# Revit family: Louver-Channel_Frame-Carnes-Rectangular-Motorized_Damper_FPJB
name_source: partatom
category: Air Terminals
revit_build: Autodesk Revit MEP 2012 (Build: 20110916_2132(x64)
units: mm (PartAtom-declared; Revit-internal decimal feet)

## types (1)
- (See Type Catalog)
    04 CSI = 08 91 00
    95 CSI = 10200
    Airflow = 0 CFM
    Assembly Code = D3090700
    Blade Material = Aluminum - Carnes - Extruded
    Catalog URL = http://www.carnes.com
    Connector Description 1 = Duct Connetor
    Default Elevation = 48"
    Description = Combination Louver / Damper
    Frame Material = Aluminum - Carnes - Extruded
    Free Area = 0 SF
    Free Area Note = See Spec Sheet URL
    Louver Height = 60"
    Louver Height Control = 60"
    Louver Length = 6 1/2"
    Louver Width = 60"
    Louver Width Control = 60"
    Manufacturer = Carnes Company
    Manufacturer Fax = 608-845-6470
    Maximum Horinzontal Size = 60"W x 120"H
    Maximum Size Note = Factory assembled multi-section max: 96”w x 120”h. Larger sizes are field assembled. Drainable blade louvers should be limited to 10’ maximum section widths (no more than 10’ between vertical downspouts) to enable the drainable design to function effectively.
    Maximum Vertical Size = 60"W x 120"H
    Meets Building Code Standards = Licensed to bear the AMCA seal
    Minimum Size = 12"W x 12"H
    Model = FPJB
    Outside Height = 60 1/2"
    Outside Width = 60 1/2"
    Point of Water Penetration = 1250 FPM
    Pressure Drop = 0.00 Pa
    Product Line = Combination Louver / Damper
    Product Page URL = http://www.carnes.com
    Specifications  URL = http://www.carnes.com
    Subcategory = Louvers and Dampers
    URL = http://www.carnes.com
    ecoScorecard Product Page = http://ecoscorecard.com

## geometry (parser evidence)
native form markers: Sweep x5
no freeform markers — native parametric forms only
